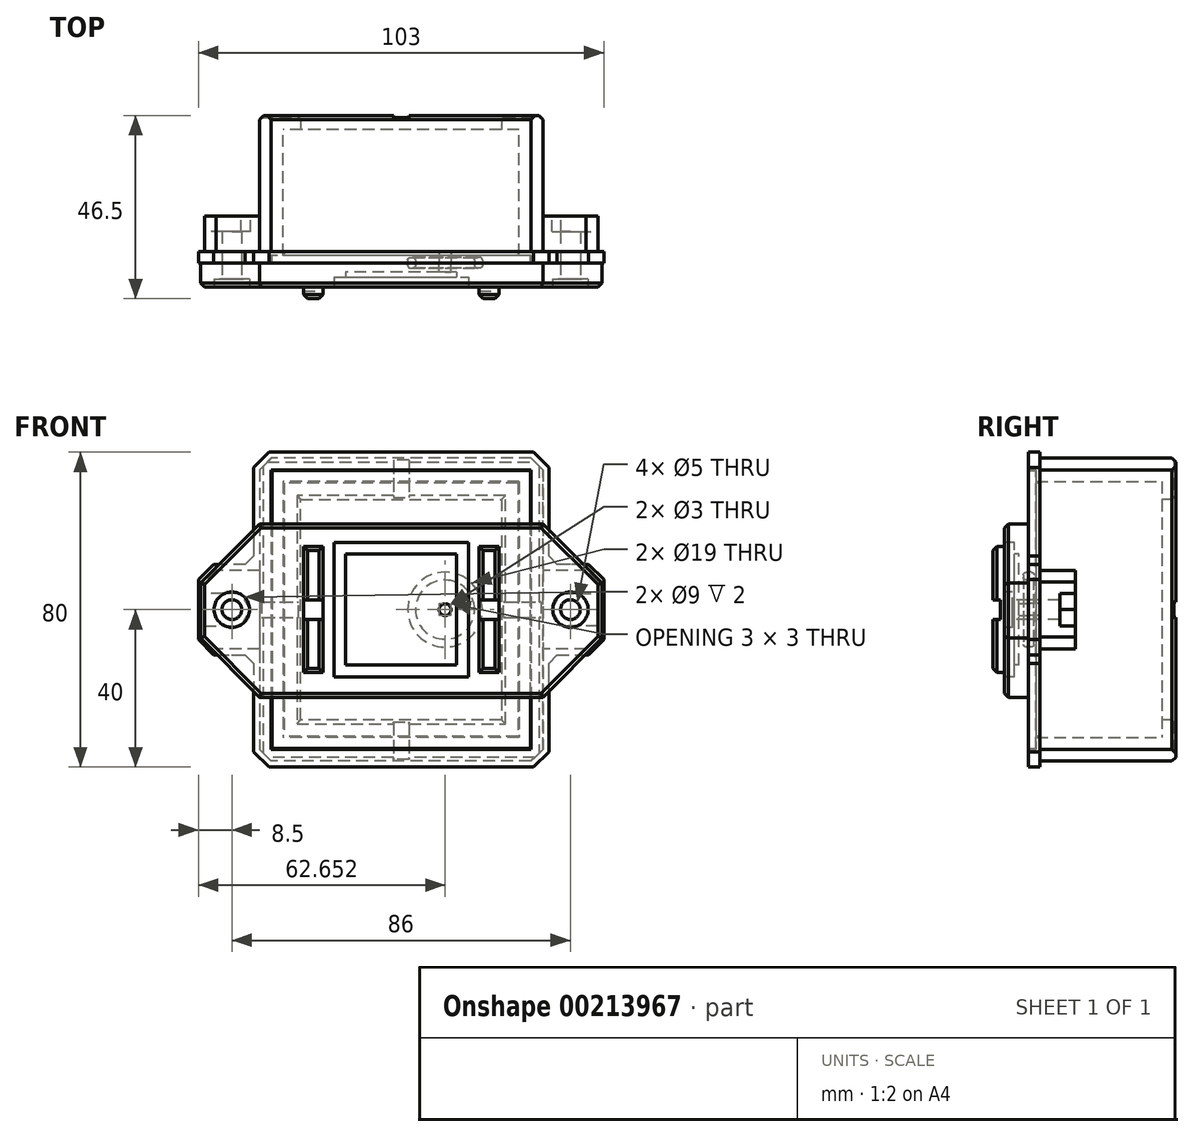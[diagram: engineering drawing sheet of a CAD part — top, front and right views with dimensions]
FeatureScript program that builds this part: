
annotation { "Feature Type Name" : "Feature", "Feature Type Description" : "" }
export const myFeature = defineFeature(function(context is Context, id is Id, definition is map)
    precondition{}
    {
        {
            var Q0;
            Q0=qCreatedBy(makeId("Front.planeOp"),FACE);
            var sketch = newSketch(context, id + "F0", { "sketchPlane" : qUnion([Q0])});
            skLineSegment(sketch, "E0.bottom", {"start": v(30, 32.5) * mm, "end": v(-30, 32.5) * mm});
            skLineSegment(sketch, "E0.top", {"start": v(30, -32.5) * mm, "end": v(-30, -32.5) * mm});
            skLineSegment(sketch, "E0.left", {"start": v(30, 32.5) * mm, "end": v(30, -32.5) * mm});
            skLineSegment(sketch, "E0.right", {"start": v(-30, 32.5) * mm, "end": v(-30, -32.5) * mm});
            skPoint(sketch, "E0.middle", {"position": v(0, 0) * mm});
            skLineSegment(sketch, "E1.0", {"start": v(36, -38.5) * mm, "end": v(-36, -38.5) * mm});
            skLineSegment(sketch, "E1.1", {"start": v(36, 38.5) * mm, "end": v(36, -38.5) * mm});
            skLineSegment(sketch, "E1.2", {"start": v(36, 38.5) * mm, "end": v(-36, 38.5) * mm});
            skLineSegment(sketch, "E1.3", {"start": v(-36, 38.5) * mm, "end": v(-36, -38.5) * mm});
            skSolve(sketch);
        }
        {
            var Q0;
            Q0 = qSketchRegion(id + "F0", true);
            extrude(context, id + "F1", {"entities" : qUnion([Q0]), "depth" : 34 * mm});
        }
        {
            var Q0;
            Q0=makeQuery(id+"F1.opExtrude","CAP_FACE",FACE,{"disambiguationData":[OSD([sQuery(id+"F0.wireOp",EDGE,"E0.bottom"),sQuery(id+"F0.wireOp",EDGE,"E0.top"),sQuery(id+"F0.wireOp",EDGE,"E0.left"),sQuery(id+"F0.wireOp",EDGE,"E0.right"),sQuery(id+"F0.wireOp",EDGE,"E1.0"),sQuery(id+"F0.wireOp",EDGE,"E1.1"),sQuery(id+"F0.wireOp",EDGE,"E1.2"),sQuery(id+"F0.wireOp",EDGE,"E1.3")])],"isStart":true});
            var sketch = newSketch(context, id + "F2", { "sketchPlane" : qUnion([Q0])});
            skLineSegment(sketch, "E2.bottom", {"start": v(-36, -38.5) * mm, "end": v(36, -38.5) * mm});
            skLineSegment(sketch, "E2.top", {"start": v(-36, 38.5) * mm, "end": v(36, 38.5) * mm});
            skLineSegment(sketch, "E2.left", {"start": v(-36, -38.5) * mm, "end": v(-36, 38.5) * mm});
            skLineSegment(sketch, "E2.right", {"start": v(36, -38.5) * mm, "end": v(36, 38.5) * mm});
            skLineSegment(sketch, "E3.0", {"start": v(-25.5, -28) * mm, "end": v(25.5, -28) * mm});
            skLineSegment(sketch, "E3.1", {"start": v(-25.5, 28) * mm, "end": v(-25.5, -28) * mm});
            skLineSegment(sketch, "E3.2", {"start": v(-25.5, 28) * mm, "end": v(25.5, 28) * mm});
            skLineSegment(sketch, "E3.3", {"start": v(25.5, 28) * mm, "end": v(25.5, -28) * mm});
            skSolve(sketch);
        }
        {
            var Q0;
            Q0 = qSketchRegion(id + "F2", true);
            extrude(context, id + "F3", {"entities" : qUnion([Q0]), "operationType" : NewBodyOperationType.ADD, "depth" : 3.5 * mm});
        }
        {
            var Q0;
            Q0=makeQuery(id+"F3.opExtrude","CAP_FACE",FACE,{"disambiguationData":[OSD([sQuery(id+"F2.wireOp",EDGE,"E2.bottom"),sQuery(id+"F2.wireOp",EDGE,"E2.top"),sQuery(id+"F2.wireOp",EDGE,"E2.left"),sQuery(id+"F2.wireOp",EDGE,"E2.right"),sQuery(id+"F2.wireOp",EDGE,"E3.0"),sQuery(id+"F2.wireOp",EDGE,"E3.1"),sQuery(id+"F2.wireOp",EDGE,"E3.2"),sQuery(id+"F2.wireOp",EDGE,"E3.3")])],"isStart":false});
            chamfer(context, id + "F4", {"entities" : qUnion([Q0]), "width" : 1 * mm, "tangentPropagation" : true});
        }
        {
            var Q0;
            Q0=makeQuery(id+"F3.boolean.opBoolean","MERGE",EDGE,{"derivedFrom":[makeQuery(id+"F1.opExtrude","SWEPT_EDGE",EDGE,{"disambiguationData":[OSD([sQuery(id+"F0.wireOp",EDGE,"E1.2"),sQuery(id+"F0.wireOp",EDGE,"E1.3")])]}),makeQuery(id+"F3.opExtrude","SWEPT_EDGE",EDGE,{"disambiguationData":[OSD([sQuery(id+"F2.wireOp",EDGE,"E2.top"),sQuery(id+"F2.wireOp",EDGE,"E2.right")])]})]});
            var Q1;
            Q1=makeQuery(id+"F3.boolean.opBoolean","MERGE",EDGE,{"derivedFrom":[makeQuery(id+"F1.opExtrude","SWEPT_EDGE",EDGE,{"disambiguationData":[OSD([sQuery(id+"F0.wireOp",EDGE,"E1.1"),sQuery(id+"F0.wireOp",EDGE,"E1.2")])]}),makeQuery(id+"F3.opExtrude","SWEPT_EDGE",EDGE,{"disambiguationData":[OSD([sQuery(id+"F2.wireOp",EDGE,"E2.top"),sQuery(id+"F2.wireOp",EDGE,"E2.left")])]})]});
            var Q2;
            Q2=makeQuery(id+"F3.boolean.opBoolean","MERGE",EDGE,{"derivedFrom":[makeQuery(id+"F1.opExtrude","SWEPT_EDGE",EDGE,{"disambiguationData":[OSD([sQuery(id+"F0.wireOp",EDGE,"E1.0"),sQuery(id+"F0.wireOp",EDGE,"E1.1")])]}),makeQuery(id+"F3.opExtrude","SWEPT_EDGE",EDGE,{"disambiguationData":[OSD([sQuery(id+"F2.wireOp",EDGE,"E2.bottom"),sQuery(id+"F2.wireOp",EDGE,"E2.left")])]})]});
            var Q3;
            Q3=makeQuery(id+"F3.boolean.opBoolean","MERGE",EDGE,{"derivedFrom":[makeQuery(id+"F1.opExtrude","SWEPT_EDGE",EDGE,{"disambiguationData":[OSD([sQuery(id+"F0.wireOp",EDGE,"E1.0"),sQuery(id+"F0.wireOp",EDGE,"E1.3")])]}),makeQuery(id+"F3.opExtrude","SWEPT_EDGE",EDGE,{"disambiguationData":[OSD([sQuery(id+"F2.wireOp",EDGE,"E2.bottom"),sQuery(id+"F2.wireOp",EDGE,"E2.right")])]})]});
            chamfer(context, id + "F5", {"entities" : qUnion([Q0, Q1, Q2, Q3]), "width" : 3 * mm, "tangentPropagation" : true});
        }
        {
            var Q0;
            Q0=makeQuery(id+"F1.opExtrude","CAP_FACE",FACE,{"disambiguationData":[OSD([sQuery(id+"F0.wireOp",EDGE,"E0.bottom"),sQuery(id+"F0.wireOp",EDGE,"E0.top"),sQuery(id+"F0.wireOp",EDGE,"E0.left"),sQuery(id+"F0.wireOp",EDGE,"E0.right"),sQuery(id+"F0.wireOp",EDGE,"E1.0"),sQuery(id+"F0.wireOp",EDGE,"E1.1"),sQuery(id+"F0.wireOp",EDGE,"E1.2"),sQuery(id+"F0.wireOp",EDGE,"E1.3")])],"isStart":false});
            var sketch = newSketch(context, id + "F6", { "sketchPlane" : qUnion([Q0])});
            skLineSegment(sketch, "E4", {"start": v(0, 0) * mm, "end": v(-36, 0) * mm, "construction": true});
            skLineSegment(sketch, "E5.bottom", {"start": v(-50, -10) * mm, "end": v(-36, -10) * mm});
            skLineSegment(sketch, "E5.top", {"start": v(-50, 10) * mm, "end": v(-36, 10) * mm});
            skLineSegment(sketch, "E5.left", {"start": v(-50, -10) * mm, "end": v(-50, 10) * mm});
            skLineSegment(sketch, "E5.right", {"start": v(-36, -10) * mm, "end": v(-36, 10) * mm});
            skPoint(sketch, "E5.middle", {"position": v(-43, 0) * mm});
            skSolve(sketch);
        }
        {
            var Q0;
            Q0 = qSketchRegion(id + "F6", true);
            extrude(context, id + "F7", {"entities" : qUnion([Q0]), "oppositeDirection" : true, "depth" : 12 * mm});
        }
        {
            var Q0;
            Q0=makeQuery(id+"F7.opExtrude","CAP_FACE",FACE,{"disambiguationData":[OSD([sQuery(id+"F6.wireOp",EDGE,"E5.bottom"),sQuery(id+"F6.wireOp",EDGE,"E5.top"),sQuery(id+"F6.wireOp",EDGE,"E5.left"),sQuery(id+"F6.wireOp",EDGE,"E5.right")])],"isStart":false});
            var sketch = newSketch(context, id + "F8", { "sketchPlane" : qUnion([Q0])});
            skLineSegment(sketch, "E6", {"start": v(50, 0) * mm, "end": v(43, 0) * mm, "construction": true});
            skPoint(sketch, "E6.endSnap0", {"position": v(50, 0) * mm});
            skCircle(sketch, "E7.cCircle", {"center": v(43, 0) * mm, "radius": 4.1 * mm, "construction": true});
            skLineSegment(sketch, "E7.0", {"start": v(45.37, -4.1) * mm, "end": v(40.63, -4.1) * mm});
            skLineSegment(sketch, "E7.1", {"start": v(40.63, -4.1) * mm, "end": v(38.27, 0) * mm});
            skLineSegment(sketch, "E7.2", {"start": v(38.27, 0) * mm, "end": v(40.63, 4.1) * mm});
            skLineSegment(sketch, "E7.3", {"start": v(40.63, 4.1) * mm, "end": v(45.37, 4.1) * mm});
            skLineSegment(sketch, "E7.4", {"start": v(45.37, 4.1) * mm, "end": v(47.73, 0) * mm, "construction": true});
            skLineSegment(sketch, "E7.5", {"start": v(47.73, 0) * mm, "end": v(45.37, -4.1) * mm, "construction": true});
            skPoint(sketch, "E7.0.midPoint", {"position": v(43, -4.1) * mm});
            skLineSegment(sketch, "E8.bottom", {"start": v(45.37, 4.1) * mm, "end": v(50, 4.1) * mm});
            skLineSegment(sketch, "E8.top", {"start": v(45.37, -4.1) * mm, "end": v(50, -4.1) * mm});
            skLineSegment(sketch, "E8.left", {"start": v(45.37, 4.1) * mm, "end": v(45.37, -4.1) * mm, "construction": true});
            skLineSegment(sketch, "E8.right", {"start": v(50, 4.1) * mm, "end": v(50, -4.1) * mm});
            skSolve(sketch);
        }
        {
            var Q0;
            Q0 = qSketchRegion(id + "F8", true);
            extrude(context, id + "F9", {"entities" : qUnion([Q0]), "operationType" : NewBodyOperationType.REMOVE, "oppositeDirection" : true, "depth" : 4 * mm});
        }
        {
            var Q0;
            Q0=makeQuery(id+"F7.boolean.opBoolean","MERGE",FACE,{"derivedFrom":[makeQuery(id+"F1.opExtrude","CAP_FACE",FACE,{"disambiguationData":[OSD([sQuery(id+"F0.wireOp",EDGE,"E0.bottom"),sQuery(id+"F0.wireOp",EDGE,"E0.top"),sQuery(id+"F0.wireOp",EDGE,"E0.left"),sQuery(id+"F0.wireOp",EDGE,"E0.right"),sQuery(id+"F0.wireOp",EDGE,"E1.0"),sQuery(id+"F0.wireOp",EDGE,"E1.1"),sQuery(id+"F0.wireOp",EDGE,"E1.2"),sQuery(id+"F0.wireOp",EDGE,"E1.3")])],"isStart":false}),makeQuery(id+"F7.opExtrude","CAP_FACE",FACE,{"disambiguationData":[OSD([sQuery(id+"F6.wireOp",EDGE,"E5.bottom"),sQuery(id+"F6.wireOp",EDGE,"E5.top"),sQuery(id+"F6.wireOp",EDGE,"E5.left"),sQuery(id+"F6.wireOp",EDGE,"E5.right")])],"isStart":true})]});
            var sketch = newSketch(context, id + "F10", { "sketchPlane" : qUnion([Q0])});
            skLineSegment(sketch, "E9", {"start": v(0, 0) * mm, "end": v(-43, 0) * mm, "construction": true});
            skCircle(sketch, "E10", {"center": v(-43, 0) * mm, "radius": 2.5 * mm});
            skSolve(sketch);
        }
        {
            var Q0;
            Q0 = qSketchRegion(id + "F10", true);
            extrude(context, id + "F11", {"entities" : qUnion([Q0]), "operationType" : NewBodyOperationType.REMOVE, "endBound" : BoundingType.THROUGH_ALL, "oppositeDirection" : true, "depth" : 25 * mm});
        }
        {
            var Q0;
            Q0=makeQuery(id+"F7.opExtrude","SWEPT_BODY",BODY,{"disambiguationData":[OSD([sQuery(id+"F6.wireOp",EDGE,"E5.bottom"),sQuery(id+"F6.wireOp",EDGE,"E5.top"),sQuery(id+"F6.wireOp",EDGE,"E5.left"),sQuery(id+"F6.wireOp",EDGE,"E5.right")])]});
            var Q1;
            Q1=qCreatedBy(makeId("Right.planeOp"),FACE);
            mirror(context, id + "F12", {"operationType" : NewBodyOperationType.ADD, "entities" : qUnion([Q0]), "mirrorPlane" : qUnion([Q1])});
        }
        {
            var Q0;
            Q0=makeQuery(id+"F12.opPattern","COPY",EDGE,{"derivedFrom":makeQuery(id+"F7.opExtrude","SWEPT_EDGE",EDGE,{"disambiguationData":[OSD([sQuery(id+"F6.wireOp",EDGE,"E5.bottom"),sQuery(id+"F6.wireOp",EDGE,"E5.left")])]}),"instanceName":"1"});
            var Q1;
            Q1=makeQuery(id+"F12.opPattern","COPY",EDGE,{"derivedFrom":makeQuery(id+"F7.opExtrude","SWEPT_EDGE",EDGE,{"disambiguationData":[OSD([sQuery(id+"F0.wireOp",EDGE,"E1.3"),sQuery(id+"F6.wireOp",EDGE,"E5.bottom"),sQuery(id+"F6.wireOp",EDGE,"E5.right")])]}),"instanceName":"1"});
            var Q2;
            Q2=makeQuery(id+"F12.opPattern","COPY",EDGE,{"derivedFrom":makeQuery(id+"F7.opExtrude","SWEPT_EDGE",EDGE,{"disambiguationData":[OSD([sQuery(id+"F6.wireOp",EDGE,"E5.top"),sQuery(id+"F6.wireOp",EDGE,"E5.left")])]}),"instanceName":"1"});
            var Q3;
            Q3=makeQuery(id+"F12.opPattern","COPY",EDGE,{"derivedFrom":makeQuery(id+"F7.opExtrude","SWEPT_EDGE",EDGE,{"disambiguationData":[OSD([sQuery(id+"F0.wireOp",EDGE,"E1.3"),sQuery(id+"F6.wireOp",EDGE,"E5.top"),sQuery(id+"F6.wireOp",EDGE,"E5.right")])]}),"instanceName":"1"});
            var Q4;
            Q4=makeQuery(id+"F7.opExtrude","SWEPT_EDGE",EDGE,{"disambiguationData":[OSD([sQuery(id+"F0.wireOp",EDGE,"E1.3"),sQuery(id+"F6.wireOp",EDGE,"E5.top"),sQuery(id+"F6.wireOp",EDGE,"E5.right")])]});
            var Q5;
            Q5=makeQuery(id+"F7.opExtrude","SWEPT_EDGE",EDGE,{"disambiguationData":[OSD([sQuery(id+"F6.wireOp",EDGE,"E5.top"),sQuery(id+"F6.wireOp",EDGE,"E5.left")])]});
            var Q6;
            Q6=makeQuery(id+"F7.opExtrude","SWEPT_EDGE",EDGE,{"disambiguationData":[OSD([sQuery(id+"F0.wireOp",EDGE,"E1.3"),sQuery(id+"F6.wireOp",EDGE,"E5.bottom"),sQuery(id+"F6.wireOp",EDGE,"E5.right")])]});
            var Q7;
            Q7=makeQuery(id+"F7.opExtrude","SWEPT_EDGE",EDGE,{"disambiguationData":[OSD([sQuery(id+"F6.wireOp",EDGE,"E5.bottom"),sQuery(id+"F6.wireOp",EDGE,"E5.left")])]});
            chamfer(context, id + "F13", {"entities" : qUnion([Q0, Q1, Q2, Q3, Q4, Q5, Q6, Q7]), "width" : 3 * mm, "tangentPropagation" : true});
        }
        {
            var Q0;
            Q0=makeQuery(id+"F3.opExtrude","CAP_FACE",FACE,{"disambiguationData":[OSD([sQuery(id+"F2.wireOp",EDGE,"E2.bottom"),sQuery(id+"F2.wireOp",EDGE,"E2.top"),sQuery(id+"F2.wireOp",EDGE,"E2.left"),sQuery(id+"F2.wireOp",EDGE,"E2.right"),sQuery(id+"F2.wireOp",EDGE,"E3.0"),sQuery(id+"F2.wireOp",EDGE,"E3.1"),sQuery(id+"F2.wireOp",EDGE,"E3.2"),sQuery(id+"F2.wireOp",EDGE,"E3.3")])],"isStart":false});
            var sketch = newSketch(context, id + "F14", { "sketchPlane" : qUnion([Q0])});
            skLineSegment(sketch, "E11.bottom", {"start": v(2, 48.52) * mm, "end": v(-2, 48.52) * mm});
            skLineSegment(sketch, "E11.top", {"start": v(2, -48.52) * mm, "end": v(-2, -48.52) * mm});
            skLineSegment(sketch, "E11.left", {"start": v(2, 48.52) * mm, "end": v(2, -48.52) * mm});
            skLineSegment(sketch, "E11.right", {"start": v(-2, 48.52) * mm, "end": v(-2, -48.52) * mm});
            skPoint(sketch, "E11.middle", {"position": v(0, 0) * mm});
            skLineSegment(sketch, "E12.bottom", {"start": v(65.48, 2) * mm, "end": v(-65.48, 2) * mm});
            skLineSegment(sketch, "E12.top", {"start": v(65.48, -2) * mm, "end": v(-65.48, -2) * mm});
            skLineSegment(sketch, "E12.left", {"start": v(65.48, 2) * mm, "end": v(65.48, -2) * mm});
            skLineSegment(sketch, "E12.right", {"start": v(-65.48, 2) * mm, "end": v(-65.48, -2) * mm});
            skSolve(sketch);
        }
        {
            var Q0;
            Q0 = qSketchRegion(id + "F14", true);
            extrude(context, id + "F15", {"entities" : qUnion([Q0]), "operationType" : NewBodyOperationType.REMOVE, "oppositeDirection" : true, "depth" : 0.5 * mm});
        }
        {
            var Q0;
            {var subQ0=makeQuery(id+"F7.opExtrude","CAP_FACE",FACE,{"disambiguationData":[OSD([sQuery(id+"F6.wireOp",EDGE,"E5.bottom"),sQuery(id+"F6.wireOp",EDGE,"E5.top"),sQuery(id+"F6.wireOp",EDGE,"E5.left"),sQuery(id+"F6.wireOp",EDGE,"E5.right")])],"isStart":true});Q0=makeQuery(id+"F12.boolean.opBoolean","MERGE",FACE,{"derivedFrom":[makeQuery(id+"F1.opExtrude","CAP_FACE",FACE,{"disambiguationData":[OSD([sQuery(id+"F0.wireOp",EDGE,"E0.bottom"),sQuery(id+"F0.wireOp",EDGE,"E0.top"),sQuery(id+"F0.wireOp",EDGE,"E0.left"),sQuery(id+"F0.wireOp",EDGE,"E0.right"),sQuery(id+"F0.wireOp",EDGE,"E1.0"),sQuery(id+"F0.wireOp",EDGE,"E1.1"),sQuery(id+"F0.wireOp",EDGE,"E1.2"),sQuery(id+"F0.wireOp",EDGE,"E1.3")])],"isStart":false}),subQ0,makeQuery(id+"F12.opPattern","COPY",FACE,{"derivedFrom":subQ0,"instanceName":"1"})]});}
            var sketch = newSketch(context, id + "F16", { "sketchPlane" : qUnion([Q0])});
            skLineSegment(sketch, "E13.0", {"start": v(-47.62, 11.5) * mm, "end": v(-51.5, 7.62) * mm});
            skLineSegment(sketch, "E13.1", {"start": v(39.62, -11.5) * mm, "end": v(47.62, -11.5) * mm});
            skLineSegment(sketch, "E13.2", {"start": v(37.5, -13.62) * mm, "end": v(39.62, -11.5) * mm});
            skLineSegment(sketch, "E13.3", {"start": v(37.5, -36.12) * mm, "end": v(37.5, -13.62) * mm});
            skLineSegment(sketch, "E13.4", {"start": v(33.62, -40) * mm, "end": v(37.5, -36.12) * mm});
            skLineSegment(sketch, "E13.5", {"start": v(-33.62, -40) * mm, "end": v(33.62, -40) * mm});
            skLineSegment(sketch, "E13.6", {"start": v(-37.5, -36.12) * mm, "end": v(-33.62, -40) * mm});
            skLineSegment(sketch, "E13.7", {"start": v(-51.5, -7.62) * mm, "end": v(-47.62, -11.5) * mm});
            skLineSegment(sketch, "E13.8", {"start": v(-47.62, -11.5) * mm, "end": v(-39.62, -11.5) * mm});
            skLineSegment(sketch, "E13.9", {"start": v(-39.62, -11.5) * mm, "end": v(-37.5, -13.62) * mm});
            skLineSegment(sketch, "E13.10", {"start": v(-37.5, -13.62) * mm, "end": v(-37.5, -36.12) * mm});
            skLineSegment(sketch, "E13.11", {"start": v(47.62, -11.5) * mm, "end": v(51.5, -7.62) * mm});
            skLineSegment(sketch, "E13.12", {"start": v(-51.5, 7.62) * mm, "end": v(-51.5, -7.62) * mm});
            skLineSegment(sketch, "E13.13", {"start": v(51.5, -7.62) * mm, "end": v(51.5, 7.62) * mm});
            skLineSegment(sketch, "E13.14", {"start": v(51.5, 7.62) * mm, "end": v(47.62, 11.5) * mm});
            skLineSegment(sketch, "E13.15", {"start": v(47.62, 11.5) * mm, "end": v(39.62, 11.5) * mm});
            skLineSegment(sketch, "E13.16", {"start": v(39.62, 11.5) * mm, "end": v(37.5, 13.62) * mm});
            skLineSegment(sketch, "E13.17", {"start": v(37.5, 13.62) * mm, "end": v(37.5, 36.12) * mm});
            skLineSegment(sketch, "E13.18", {"start": v(37.5, 36.12) * mm, "end": v(33.62, 40) * mm});
            skLineSegment(sketch, "E13.19", {"start": v(33.62, 40) * mm, "end": v(-33.62, 40) * mm});
            skLineSegment(sketch, "E13.20", {"start": v(-33.62, 40) * mm, "end": v(-37.5, 36.12) * mm});
            skLineSegment(sketch, "E13.21", {"start": v(-37.5, 36.12) * mm, "end": v(-37.5, 13.62) * mm});
            skLineSegment(sketch, "E13.22", {"start": v(-37.5, 13.62) * mm, "end": v(-39.62, 11.5) * mm});
            skLineSegment(sketch, "E13.23", {"start": v(-39.62, 11.5) * mm, "end": v(-47.62, 11.5) * mm});
            skCircle(sketch, "E14.0", {"center": v(-43, 0) * mm, "radius": 2.5 * mm});
            skCircle(sketch, "E15.0", {"center": v(43, 0) * mm, "radius": 2.5 * mm});
            skLineSegment(sketch, "E16.0", {"start": v(-30, 32.5) * mm, "end": v(-30, -32.5) * mm});
            skLineSegment(sketch, "E16.1", {"start": v(30, -32.5) * mm, "end": v(-30, -32.5) * mm});
            skLineSegment(sketch, "E16.2", {"start": v(30, 32.5) * mm, "end": v(-30, 32.5) * mm});
            skLineSegment(sketch, "E16.3", {"start": v(30, 32.5) * mm, "end": v(30, -32.5) * mm});
            skSolve(sketch);
        }
        {
            var Q0;
            Q0 = qSketchRegion(id + "F16", true);
            extrude(context, id + "F17", {"entities" : qUnion([Q0]), "operationType" : NewBodyOperationType.ADD, "oppositeDirection" : true, "depth" : 3 * mm});
        }
        {
            var Q0;
            {var subQ0=makeQuery(id+"F7.opExtrude","CAP_FACE",FACE,{"disambiguationData":[OSD([sQuery(id+"F6.wireOp",EDGE,"E5.bottom"),sQuery(id+"F6.wireOp",EDGE,"E5.top"),sQuery(id+"F6.wireOp",EDGE,"E5.left"),sQuery(id+"F6.wireOp",EDGE,"E5.right")])],"isStart":true});Q0=makeQuery(id+"F17.boolean.opBoolean","MERGE",FACE,{"derivedFrom":[makeQuery(id+"F12.boolean.opBoolean","MERGE",FACE,{"derivedFrom":[makeQuery(id+"F1.opExtrude","CAP_FACE",FACE,{"disambiguationData":[OSD([sQuery(id+"F0.wireOp",EDGE,"E0.bottom"),sQuery(id+"F0.wireOp",EDGE,"E0.top"),sQuery(id+"F0.wireOp",EDGE,"E0.left"),sQuery(id+"F0.wireOp",EDGE,"E0.right"),sQuery(id+"F0.wireOp",EDGE,"E1.0"),sQuery(id+"F0.wireOp",EDGE,"E1.1"),sQuery(id+"F0.wireOp",EDGE,"E1.2"),sQuery(id+"F0.wireOp",EDGE,"E1.3")])],"isStart":false}),subQ0,makeQuery(id+"F12.opPattern","COPY",FACE,{"derivedFrom":subQ0,"instanceName":"1"})]}),makeQuery(id+"F17.opExtrude","CAP_FACE",FACE,{"disambiguationData":[OSD([sQuery(id+"F16.wireOp",EDGE,"E13.0"),sQuery(id+"F16.wireOp",EDGE,"E13.1"),sQuery(id+"F16.wireOp",EDGE,"E13.2"),sQuery(id+"F16.wireOp",EDGE,"E13.3"),sQuery(id+"F16.wireOp",EDGE,"E13.4"),sQuery(id+"F16.wireOp",EDGE,"E13.5"),sQuery(id+"F16.wireOp",EDGE,"E13.6"),sQuery(id+"F16.wireOp",EDGE,"E13.7"),sQuery(id+"F16.wireOp",EDGE,"E13.8"),sQuery(id+"F16.wireOp",EDGE,"E13.9"),sQuery(id+"F16.wireOp",EDGE,"E13.10"),sQuery(id+"F16.wireOp",EDGE,"E13.11"),sQuery(id+"F16.wireOp",EDGE,"E13.12"),sQuery(id+"F16.wireOp",EDGE,"E13.13"),sQuery(id+"F16.wireOp",EDGE,"E13.14"),sQuery(id+"F16.wireOp",EDGE,"E13.15"),sQuery(id+"F16.wireOp",EDGE,"E13.16"),sQuery(id+"F16.wireOp",EDGE,"E13.17"),sQuery(id+"F16.wireOp",EDGE,"E13.18"),sQuery(id+"F16.wireOp",EDGE,"E13.19"),sQuery(id+"F16.wireOp",EDGE,"E13.20"),sQuery(id+"F16.wireOp",EDGE,"E13.21"),sQuery(id+"F16.wireOp",EDGE,"E13.22"),sQuery(id+"F16.wireOp",EDGE,"E13.23"),sQuery(id+"F16.wireOp",EDGE,"E14.0"),sQuery(id+"F16.wireOp",EDGE,"E15.0"),sQuery(id+"F16.wireOp",EDGE,"E16.0"),sQuery(id+"F16.wireOp",EDGE,"E16.1"),sQuery(id+"F16.wireOp",EDGE,"E16.2"),sQuery(id+"F16.wireOp",EDGE,"E16.3")])],"isStart":true})]});}
            var sketch = newSketch(context, id + "F18", { "sketchPlane" : qUnion([Q0])});
            skLineSegment(sketch, "E17.0", {"start": v(33, 35.5) * mm, "end": v(-33, 35.5) * mm});
            skLineSegment(sketch, "E17.1", {"start": v(33, 35.5) * mm, "end": v(33, -35.5) * mm});
            skLineSegment(sketch, "E17.2", {"start": v(33, -35.5) * mm, "end": v(-33, -35.5) * mm});
            skLineSegment(sketch, "E17.3", {"start": v(-33, 35.5) * mm, "end": v(-33, -35.5) * mm});
            skSolve(sketch);
        }
        {
            var Q0;
            Q0 = qSketchRegion(id + "F18", true);
            extrude(context, id + "F19", {"entities" : qUnion([Q0]), "operationType" : NewBodyOperationType.REMOVE, "oppositeDirection" : true, "depth" : 2 * mm});
        }
        {
            var Q0;
            Q0=makeQuery(id+"F19.boolean.opBoolean","COPY",FACE,{"derivedFrom":makeQuery(id+"F19.opExtrude","CAP_FACE",FACE,{"disambiguationData":[OSD([sQuery(id+"F18.wireOp",EDGE,"E17.0"),sQuery(id+"F18.wireOp",EDGE,"E17.1"),sQuery(id+"F18.wireOp",EDGE,"E17.2"),sQuery(id+"F18.wireOp",EDGE,"E17.3")])],"isStart":false})});
            var sketch = newSketch(context, id + "F20", { "sketchPlane" : qUnion([Q0])});
            skLineSegment(sketch, "E18.0", {"start": v(32.8, 35.3) * mm, "end": v(-32.8, 35.3) * mm});
            skLineSegment(sketch, "E18.1", {"start": v(32.8, -35.3) * mm, "end": v(32.8, 35.3) * mm});
            skLineSegment(sketch, "E18.2", {"start": v(-32.8, -35.3) * mm, "end": v(32.8, -35.3) * mm});
            skLineSegment(sketch, "E18.3", {"start": v(-32.8, 35.3) * mm, "end": v(-32.8, -35.3) * mm});
            skSolve(sketch);
        }
        {
            var Q0;
            Q0 = qSketchRegion(id + "F20", true);
            var Q1;
            {var subQ0=makeQuery(id+"F7.opExtrude","CAP_FACE",FACE,{"disambiguationData":[OSD([sQuery(id+"F6.wireOp",EDGE,"E5.bottom"),sQuery(id+"F6.wireOp",EDGE,"E5.top"),sQuery(id+"F6.wireOp",EDGE,"E5.left"),sQuery(id+"F6.wireOp",EDGE,"E5.right")])],"isStart":true});Q1=makeQuery(id+"F17.boolean.opBoolean","MERGE",FACE,{"derivedFrom":[makeQuery(id+"F12.boolean.opBoolean","MERGE",FACE,{"derivedFrom":[makeQuery(id+"F1.opExtrude","CAP_FACE",FACE,{"disambiguationData":[OSD([sQuery(id+"F0.wireOp",EDGE,"E0.bottom"),sQuery(id+"F0.wireOp",EDGE,"E0.top"),sQuery(id+"F0.wireOp",EDGE,"E0.left"),sQuery(id+"F0.wireOp",EDGE,"E0.right"),sQuery(id+"F0.wireOp",EDGE,"E1.0"),sQuery(id+"F0.wireOp",EDGE,"E1.1"),sQuery(id+"F0.wireOp",EDGE,"E1.2"),sQuery(id+"F0.wireOp",EDGE,"E1.3")])],"isStart":false}),subQ0,makeQuery(id+"F12.opPattern","COPY",FACE,{"derivedFrom":subQ0,"instanceName":"1"})]}),makeQuery(id+"F17.opExtrude","CAP_FACE",FACE,{"disambiguationData":[OSD([sQuery(id+"F16.wireOp",EDGE,"E13.0"),sQuery(id+"F16.wireOp",EDGE,"E13.1"),sQuery(id+"F16.wireOp",EDGE,"E13.2"),sQuery(id+"F16.wireOp",EDGE,"E13.3"),sQuery(id+"F16.wireOp",EDGE,"E13.4"),sQuery(id+"F16.wireOp",EDGE,"E13.5"),sQuery(id+"F16.wireOp",EDGE,"E13.6"),sQuery(id+"F16.wireOp",EDGE,"E13.7"),sQuery(id+"F16.wireOp",EDGE,"E13.8"),sQuery(id+"F16.wireOp",EDGE,"E13.9"),sQuery(id+"F16.wireOp",EDGE,"E13.10"),sQuery(id+"F16.wireOp",EDGE,"E13.11"),sQuery(id+"F16.wireOp",EDGE,"E13.12"),sQuery(id+"F16.wireOp",EDGE,"E13.13"),sQuery(id+"F16.wireOp",EDGE,"E13.14"),sQuery(id+"F16.wireOp",EDGE,"E13.15"),sQuery(id+"F16.wireOp",EDGE,"E13.16"),sQuery(id+"F16.wireOp",EDGE,"E13.17"),sQuery(id+"F16.wireOp",EDGE,"E13.18"),sQuery(id+"F16.wireOp",EDGE,"E13.19"),sQuery(id+"F16.wireOp",EDGE,"E13.20"),sQuery(id+"F16.wireOp",EDGE,"E13.21"),sQuery(id+"F16.wireOp",EDGE,"E13.22"),sQuery(id+"F16.wireOp",EDGE,"E13.23"),sQuery(id+"F16.wireOp",EDGE,"E14.0"),sQuery(id+"F16.wireOp",EDGE,"E15.0"),sQuery(id+"F16.wireOp",EDGE,"E16.0"),sQuery(id+"F16.wireOp",EDGE,"E16.1"),sQuery(id+"F16.wireOp",EDGE,"E16.2"),sQuery(id+"F16.wireOp",EDGE,"E16.3")])],"isStart":true})]});}
            extrude(context, id + "F21", {"entities" : qUnion([Q0]), "endBound" : BoundingType.UP_TO_SURFACE, "endBoundEntityFace" : qUnion([Q1]), "depth" : 25 * mm});
        }
        {
            var Q0;
            Q0=makeQuery(id+"F21.opExtrude","CAP_FACE",FACE,{"disambiguationData":[OSD([sQuery(id+"F20.wireOp",EDGE,"E18.0"),sQuery(id+"F20.wireOp",EDGE,"E18.1"),sQuery(id+"F20.wireOp",EDGE,"E18.2"),sQuery(id+"F20.wireOp",EDGE,"E18.3")])],"isStart":true});
            var sketch = newSketch(context, id + "F22", { "sketchPlane" : qUnion([Q0])});
            skLineSegment(sketch, "E19.0", {"start": v(-29.7, 32.2) * mm, "end": v(29.7, 32.2) * mm});
            skLineSegment(sketch, "E19.1", {"start": v(-29.7, 32.2) * mm, "end": v(-29.7, -32.2) * mm});
            skLineSegment(sketch, "E19.2", {"start": v(-29.7, -32.2) * mm, "end": v(29.7, -32.2) * mm});
            skLineSegment(sketch, "E19.3", {"start": v(29.7, 32.2) * mm, "end": v(29.7, -32.2) * mm});
            skSolve(sketch);
        }
        {
            var Q0;
            Q0 = qSketchRegion(id + "F22", true);
            extrude(context, id + "F23", {"entities" : qUnion([Q0]), "operationType" : NewBodyOperationType.ADD, "depth" : 1 * mm});
        }
        {
            var Q0;
            Q0=makeQuery(id+"F21.opExtrude","CAP_FACE",FACE,{"disambiguationData":[OSD([sQuery(id+"F20.wireOp",EDGE,"E18.0"),sQuery(id+"F20.wireOp",EDGE,"E18.1"),sQuery(id+"F20.wireOp",EDGE,"E18.2"),sQuery(id+"F20.wireOp",EDGE,"E18.3")])],"isStart":false});
            var sketch = newSketch(context, id + "F24", { "sketchPlane" : qUnion([Q0])});
            skCircle(sketch, "E20", {"center": v(11.15, 0) * mm, "radius": 1.5 * mm});
            skSolve(sketch);
        }
        {
            var Q0;
            Q0 = qSketchRegion(id + "F24", true);
            extrude(context, id + "F25", {"entities" : qUnion([Q0]), "operationType" : NewBodyOperationType.REMOVE, "endBound" : BoundingType.THROUGH_ALL, "oppositeDirection" : true, "depth" : 25 * mm});
        }
        {
            var Q0;
            Q0=makeQuery(id+"F21.opExtrude","CAP_FACE",FACE,{"disambiguationData":[OSD([sQuery(id+"F20.wireOp",EDGE,"E18.0"),sQuery(id+"F20.wireOp",EDGE,"E18.1"),sQuery(id+"F20.wireOp",EDGE,"E18.2"),sQuery(id+"F20.wireOp",EDGE,"E18.3")])],"isStart":false});
            var sketch = newSketch(context, id + "F26", { "sketchPlane" : qUnion([Q0])});
            skCircle(sketch, "E21", {"center": v(11.15, 0) * mm, "radius": 7.5 * mm});
            skCircle(sketch, "E22", {"center": v(11.15, 0) * mm, "radius": 9.5 * mm});
            skSolve(sketch);
        }
        {
            var Q0;
            Q0 = qSketchRegion(id + "F26", true);
            extrude(context, id + "F27", {"entities" : qUnion([Q0]), "operationType" : NewBodyOperationType.REMOVE, "oppositeDirection" : true, "depth" : 1.5 * mm});
        }
        {
            var Q0;
            Q0=makeQuery(id+"F27.boolean.opBoolean","COPY",FACE,{"derivedFrom":makeQuery(id+"F27.opExtrude","CAP_FACE",FACE,{"disambiguationData":[OSD([sQuery(id+"F26.wireOp",EDGE,"E21"),sQuery(id+"F26.wireOp",EDGE,"E22")])],"isStart":false})});
            fillet(context, id + "F28", {"entities" : qUnion([Q0]), "radius" : 0.7 * mm, "tangentPropagation" : true, "allowEdgeOverflow" : false});
        }
        {
            var Q0;
            {var subQ0=makeQuery(id+"F7.opExtrude","CAP_FACE",FACE,{"disambiguationData":[OSD([sQuery(id+"F6.wireOp",EDGE,"E5.bottom"),sQuery(id+"F6.wireOp",EDGE,"E5.top"),sQuery(id+"F6.wireOp",EDGE,"E5.left"),sQuery(id+"F6.wireOp",EDGE,"E5.right")])],"isStart":true});Q0=makeQuery(id+"F17.boolean.opBoolean","MERGE",FACE,{"derivedFrom":[makeQuery(id+"F12.boolean.opBoolean","MERGE",FACE,{"derivedFrom":[makeQuery(id+"F1.opExtrude","CAP_FACE",FACE,{"disambiguationData":[OSD([sQuery(id+"F0.wireOp",EDGE,"E0.bottom"),sQuery(id+"F0.wireOp",EDGE,"E0.top"),sQuery(id+"F0.wireOp",EDGE,"E0.left"),sQuery(id+"F0.wireOp",EDGE,"E0.right"),sQuery(id+"F0.wireOp",EDGE,"E1.0"),sQuery(id+"F0.wireOp",EDGE,"E1.1"),sQuery(id+"F0.wireOp",EDGE,"E1.2"),sQuery(id+"F0.wireOp",EDGE,"E1.3")])],"isStart":false}),subQ0,makeQuery(id+"F12.opPattern","COPY",FACE,{"derivedFrom":subQ0,"instanceName":"1"})]}),makeQuery(id+"F17.opExtrude","CAP_FACE",FACE,{"disambiguationData":[OSD([sQuery(id+"F16.wireOp",EDGE,"E13.0"),sQuery(id+"F16.wireOp",EDGE,"E13.1"),sQuery(id+"F16.wireOp",EDGE,"E13.2"),sQuery(id+"F16.wireOp",EDGE,"E13.3"),sQuery(id+"F16.wireOp",EDGE,"E13.4"),sQuery(id+"F16.wireOp",EDGE,"E13.5"),sQuery(id+"F16.wireOp",EDGE,"E13.6"),sQuery(id+"F16.wireOp",EDGE,"E13.7"),sQuery(id+"F16.wireOp",EDGE,"E13.8"),sQuery(id+"F16.wireOp",EDGE,"E13.9"),sQuery(id+"F16.wireOp",EDGE,"E13.10"),sQuery(id+"F16.wireOp",EDGE,"E13.11"),sQuery(id+"F16.wireOp",EDGE,"E13.12"),sQuery(id+"F16.wireOp",EDGE,"E13.13"),sQuery(id+"F16.wireOp",EDGE,"E13.14"),sQuery(id+"F16.wireOp",EDGE,"E13.15"),sQuery(id+"F16.wireOp",EDGE,"E13.16"),sQuery(id+"F16.wireOp",EDGE,"E13.17"),sQuery(id+"F16.wireOp",EDGE,"E13.18"),sQuery(id+"F16.wireOp",EDGE,"E13.19"),sQuery(id+"F16.wireOp",EDGE,"E13.20"),sQuery(id+"F16.wireOp",EDGE,"E13.21"),sQuery(id+"F16.wireOp",EDGE,"E13.22"),sQuery(id+"F16.wireOp",EDGE,"E13.23"),sQuery(id+"F16.wireOp",EDGE,"E14.0"),sQuery(id+"F16.wireOp",EDGE,"E15.0"),sQuery(id+"F16.wireOp",EDGE,"E16.0"),sQuery(id+"F16.wireOp",EDGE,"E16.1"),sQuery(id+"F16.wireOp",EDGE,"E16.2"),sQuery(id+"F16.wireOp",EDGE,"E16.3")])],"isStart":true})]});}
            var sketch = newSketch(context, id + "F29", { "sketchPlane" : qUnion([Q0])});
            skLineSegment(sketch, "E23.bottom", {"start": v(51, 21.75) * mm, "end": v(-51, 21.75) * mm});
            skLineSegment(sketch, "E23.top", {"start": v(51, -22.25) * mm, "end": v(-51, -22.25) * mm});
            skLineSegment(sketch, "E23.left", {"start": v(51, 21.75) * mm, "end": v(51, -22.25) * mm});
            skLineSegment(sketch, "E23.right", {"start": v(-51, 21.75) * mm, "end": v(-51, -22.25) * mm});
            skPoint(sketch, "E23.middle", {"position": v(0, -0.25) * mm});
            skSolve(sketch);
        }
        {
            var Q0;
            Q0 = qSketchRegion(id + "F29", true);
            extrude(context, id + "F30", {"entities" : qUnion([Q0]), "depth" : 6 * mm});
        }
        {
            var Q0;
            Q0=makeQuery(id+"F30.opExtrude","CAP_FACE",FACE,{"disambiguationData":[OSD([sQuery(id+"F29.wireOp",EDGE,"E23.bottom"),sQuery(id+"F29.wireOp",EDGE,"E23.top"),sQuery(id+"F29.wireOp",EDGE,"E23.left"),sQuery(id+"F29.wireOp",EDGE,"E23.right")])],"isStart":false});
            var sketch = newSketch(context, id + "F31", { "sketchPlane" : qUnion([Q0])});
            skCircle(sketch, "E24.0", {"center": v(43, 0) * mm, "radius": 2.5 * mm});
            skCircle(sketch, "E24.1", {"center": v(-43, 0) * mm, "radius": 2.5 * mm});
            skSolve(sketch);
        }
        {
            var Q0;
            Q0 = qSketchRegion(id + "F31", true);
            extrude(context, id + "F32", {"entities" : qUnion([Q0]), "operationType" : NewBodyOperationType.REMOVE, "endBound" : BoundingType.THROUGH_ALL, "oppositeDirection" : true, "depth" : 25 * mm});
        }
        {
            var Q0;
            Q0=makeQuery(id+"F30.opExtrude","CAP_FACE",FACE,{"disambiguationData":[OSD([sQuery(id+"F29.wireOp",EDGE,"E23.bottom"),sQuery(id+"F29.wireOp",EDGE,"E23.top"),sQuery(id+"F29.wireOp",EDGE,"E23.left"),sQuery(id+"F29.wireOp",EDGE,"E23.right")])],"isStart":false});
            var sketch = newSketch(context, id + "F33", { "sketchPlane" : qUnion([Q0])});
            skCircle(sketch, "E25", {"center": v(-43, 0) * mm, "radius": 4.5 * mm});
            skCircle(sketch, "E26", {"center": v(43, 0) * mm, "radius": 4.5 * mm});
            skSolve(sketch);
        }
        {
            var Q0;
            Q0 = qSketchRegion(id + "F33", true);
            extrude(context, id + "F34", {"entities" : qUnion([Q0]), "operationType" : NewBodyOperationType.REMOVE, "oppositeDirection" : true, "depth" : 2 * mm});
        }
        {
            var Q0;
            Q0=makeQuery(id+"F30.opExtrude","SWEPT_EDGE",EDGE,{"disambiguationData":[OSD([sQuery(id+"F29.wireOp",EDGE,"E23.top"),sQuery(id+"F29.wireOp",EDGE,"E23.right")])]});
            var Q1;
            Q1=makeQuery(id+"F30.opExtrude","SWEPT_EDGE",EDGE,{"disambiguationData":[OSD([sQuery(id+"F29.wireOp",EDGE,"E23.top"),sQuery(id+"F29.wireOp",EDGE,"E23.left")])]});
            var Q2;
            Q2=makeQuery(id+"F30.opExtrude","SWEPT_EDGE",EDGE,{"disambiguationData":[OSD([sQuery(id+"F29.wireOp",EDGE,"E23.bottom"),sQuery(id+"F29.wireOp",EDGE,"E23.left")])]});
            var Q3;
            Q3=makeQuery(id+"F30.opExtrude","SWEPT_EDGE",EDGE,{"disambiguationData":[OSD([sQuery(id+"F29.wireOp",EDGE,"E23.bottom"),sQuery(id+"F29.wireOp",EDGE,"E23.right")])]});
            chamfer(context, id + "F35", {"entities" : qUnion([Q0, Q1, Q2, Q3]), "width" : 15 * mm, "tangentPropagation" : true});
        }
        {
            var Q0;
            Q0=makeQuery(id+"F30.opExtrude","CAP_FACE",FACE,{"disambiguationData":[OSD([sQuery(id+"F29.wireOp",EDGE,"E23.bottom"),sQuery(id+"F29.wireOp",EDGE,"E23.top"),sQuery(id+"F29.wireOp",EDGE,"E23.left"),sQuery(id+"F29.wireOp",EDGE,"E23.right")])],"isStart":false});
            var sketch = newSketch(context, id + "F36", { "sketchPlane" : qUnion([Q0])});
            skLineSegment(sketch, "E27.bottom", {"start": v(-17.1, -17.1) * mm, "end": v(17.1, -17.1) * mm});
            skLineSegment(sketch, "E27.top", {"start": v(-17.1, 17.1) * mm, "end": v(17.1, 17.1) * mm});
            skLineSegment(sketch, "E27.left", {"start": v(-17.1, -17.1) * mm, "end": v(-17.1, 17.1) * mm});
            skLineSegment(sketch, "E27.right", {"start": v(17.1, -17.1) * mm, "end": v(17.1, 17.1) * mm});
            skPoint(sketch, "E27.middle", {"position": v(0, 0) * mm});
            skSolve(sketch);
        }
        {
            var Q0;
            Q0 = qSketchRegion(id + "F36", true);
            extrude(context, id + "F37", {"entities" : qUnion([Q0]), "operationType" : NewBodyOperationType.REMOVE, "oppositeDirection" : true, "depth" : 2.5 * mm});
        }
        {
            var Q0;
            Q0=makeQuery(id+"F30.opExtrude","CAP_EDGE",EDGE,{"disambiguationData":[OSD([sQuery(id+"F29.wireOp",EDGE,"E23.top")])],"isStart":false});
            var Q1;
            {var subQ0=sQuery(id+"F29.wireOp",EDGE,"E23.right");var subQ1=sQuery(id+"F29.wireOp",EDGE,"E23.top");Q1=makeQuery(id+"F35.opChamfer","BLEND_EDGE",EDGE,{"blendedFrom":[makeQuery(id+"F30.opExtrude","SWEPT_EDGE",EDGE,{"disambiguationData":[OSD([subQ1,subQ0])]}),makeQuery(id+"F30.opExtrude","CAP_FACE",FACE,{"disambiguationData":[OSD([sQuery(id+"F29.wireOp",EDGE,"E23.bottom"),subQ1,sQuery(id+"F29.wireOp",EDGE,"E23.left"),subQ0])],"isStart":false})],"blendedInto":[makeQuery(id+"F30.opExtrude","CAP_FACE",FACE,{"disambiguationData":[OSD([sQuery(id+"F29.wireOp",EDGE,"E23.bottom"),subQ1,sQuery(id+"F29.wireOp",EDGE,"E23.left"),subQ0])],"isStart":false})]});}
            var Q2;
            Q2=makeQuery(id+"F30.opExtrude","CAP_EDGE",EDGE,{"disambiguationData":[OSD([sQuery(id+"F29.wireOp",EDGE,"E23.right")])],"isStart":false});
            var Q3;
            {var subQ0=sQuery(id+"F29.wireOp",EDGE,"E23.right");var subQ1=sQuery(id+"F29.wireOp",EDGE,"E23.bottom");Q3=makeQuery(id+"F35.opChamfer","BLEND_EDGE",EDGE,{"blendedFrom":[makeQuery(id+"F30.opExtrude","SWEPT_EDGE",EDGE,{"disambiguationData":[OSD([subQ1,subQ0])]}),makeQuery(id+"F30.opExtrude","CAP_FACE",FACE,{"disambiguationData":[OSD([subQ1,sQuery(id+"F29.wireOp",EDGE,"E23.top"),sQuery(id+"F29.wireOp",EDGE,"E23.left"),subQ0])],"isStart":false})],"blendedInto":[makeQuery(id+"F30.opExtrude","CAP_FACE",FACE,{"disambiguationData":[OSD([subQ1,sQuery(id+"F29.wireOp",EDGE,"E23.top"),sQuery(id+"F29.wireOp",EDGE,"E23.left"),subQ0])],"isStart":false})]});}
            var Q4;
            Q4=makeQuery(id+"F30.opExtrude","CAP_EDGE",EDGE,{"disambiguationData":[OSD([sQuery(id+"F29.wireOp",EDGE,"E23.bottom")])],"isStart":false});
            var Q5;
            {var subQ0=sQuery(id+"F29.wireOp",EDGE,"E23.left");var subQ1=sQuery(id+"F29.wireOp",EDGE,"E23.bottom");Q5=makeQuery(id+"F35.opChamfer","BLEND_EDGE",EDGE,{"blendedFrom":[makeQuery(id+"F30.opExtrude","SWEPT_EDGE",EDGE,{"disambiguationData":[OSD([subQ1,subQ0])]}),makeQuery(id+"F30.opExtrude","CAP_FACE",FACE,{"disambiguationData":[OSD([subQ1,sQuery(id+"F29.wireOp",EDGE,"E23.top"),subQ0,sQuery(id+"F29.wireOp",EDGE,"E23.right")])],"isStart":false})],"blendedInto":[makeQuery(id+"F30.opExtrude","CAP_FACE",FACE,{"disambiguationData":[OSD([subQ1,sQuery(id+"F29.wireOp",EDGE,"E23.top"),subQ0,sQuery(id+"F29.wireOp",EDGE,"E23.right")])],"isStart":false})]});}
            var Q6;
            Q6=makeQuery(id+"F30.opExtrude","CAP_EDGE",EDGE,{"disambiguationData":[OSD([sQuery(id+"F29.wireOp",EDGE,"E23.left")])],"isStart":false});
            var Q7;
            {var subQ0=sQuery(id+"F29.wireOp",EDGE,"E23.left");var subQ1=sQuery(id+"F29.wireOp",EDGE,"E23.top");Q7=makeQuery(id+"F35.opChamfer","BLEND_EDGE",EDGE,{"blendedFrom":[makeQuery(id+"F30.opExtrude","SWEPT_EDGE",EDGE,{"disambiguationData":[OSD([subQ1,subQ0])]}),makeQuery(id+"F30.opExtrude","CAP_FACE",FACE,{"disambiguationData":[OSD([sQuery(id+"F29.wireOp",EDGE,"E23.bottom"),subQ1,subQ0,sQuery(id+"F29.wireOp",EDGE,"E23.right")])],"isStart":false})],"blendedInto":[makeQuery(id+"F30.opExtrude","CAP_FACE",FACE,{"disambiguationData":[OSD([sQuery(id+"F29.wireOp",EDGE,"E23.bottom"),subQ1,subQ0,sQuery(id+"F29.wireOp",EDGE,"E23.right")])],"isStart":false})]});}
            chamfer(context, id + "F38", {"entities" : qUnion([Q0, Q1, Q2, Q3, Q4, Q5, Q6, Q7]), "width" : 1 * mm, "tangentPropagation" : true});
        }
        {
            var Q0;
            Q0=makeQuery(id+"F30.opExtrude","CAP_FACE",FACE,{"disambiguationData":[OSD([sQuery(id+"F29.wireOp",EDGE,"E23.bottom"),sQuery(id+"F29.wireOp",EDGE,"E23.top"),sQuery(id+"F29.wireOp",EDGE,"E23.left"),sQuery(id+"F29.wireOp",EDGE,"E23.right")])],"isStart":false});
            var sketch = newSketch(context, id + "F39", { "sketchPlane" : qUnion([Q0])});
            skLineSegment(sketch, "E28.bottom", {"start": v(19.83, -16) * mm, "end": v(24.83, -16) * mm});
            skLineSegment(sketch, "E28.top", {"start": v(19.83, 16) * mm, "end": v(24.83, 16) * mm});
            skLineSegment(sketch, "E28.left", {"start": v(19.83, -16) * mm, "end": v(19.83, 16) * mm});
            skLineSegment(sketch, "E28.right", {"start": v(24.83, -16) * mm, "end": v(24.83, 16) * mm});
            skPoint(sketch, "E28.middle", {"position": v(22.33, 0) * mm});
            skPoint(sketch, "E28.middle.positionSnap0", {"position": v(17.1, 0) * mm});
            skPoint(sketch, "E28.centerSnap0", {"position": v(17.1, 0) * mm});
            skLineSegment(sketch, "E29.MirrorCS", {"start": v(-19.83, -16) * mm, "end": v(-24.83, -16) * mm});
            skLineSegment(sketch, "E30.MirrorCS", {"start": v(-24.83, -16) * mm, "end": v(-24.83, 16) * mm});
            skLineSegment(sketch, "E31.MirrorCS", {"start": v(-19.83, -16) * mm, "end": v(-19.83, 16) * mm});
            skLineSegment(sketch, "E32.MirrorCS", {"start": v(-19.83, 16) * mm, "end": v(-24.83, 16) * mm});
            skSolve(sketch);
        }
        {
            var Q0;
            Q0 = qSketchRegion(id + "F39", true);
            extrude(context, id + "F40", {"entities" : qUnion([Q0]), "operationType" : NewBodyOperationType.ADD, "depth" : 3 * mm});
        }
        {
            var Q0;
            Q0=makeQuery(id+"F40.opExtrude","CAP_FACE",FACE,{"disambiguationData":[OSD([sQuery(id+"F39.wireOp",EDGE,"E28.bottom"),sQuery(id+"F39.wireOp",EDGE,"E28.top"),sQuery(id+"F39.wireOp",EDGE,"E28.left"),sQuery(id+"F39.wireOp",EDGE,"E28.right")])],"isStart":false});
            var Q1;
            Q1=makeQuery(id+"F40.opExtrude","CAP_FACE",FACE,{"disambiguationData":[OSD([sQuery(id+"F39.wireOp",EDGE,"E29.MirrorCS"),sQuery(id+"F39.wireOp",EDGE,"E30.MirrorCS"),sQuery(id+"F39.wireOp",EDGE,"E31.MirrorCS"),sQuery(id+"F39.wireOp",EDGE,"E32.MirrorCS")])],"isStart":false});
            chamfer(context, id + "F41", {"entities" : qUnion([Q0, Q1]), "width" : 1 * mm, "tangentPropagation" : true});
        }
        {
            var Q0;
            Q0=makeQuery(id+"F40.opExtrude","CAP_FACE",FACE,{"disambiguationData":[OSD([sQuery(id+"F39.wireOp",EDGE,"E29.MirrorCS"),sQuery(id+"F39.wireOp",EDGE,"E30.MirrorCS"),sQuery(id+"F39.wireOp",EDGE,"E31.MirrorCS"),sQuery(id+"F39.wireOp",EDGE,"E32.MirrorCS")])],"isStart":false});
            var sketch = newSketch(context, id + "F42", { "sketchPlane" : qUnion([Q0])});
            skLineSegment(sketch, "E33.bottom", {"start": v(-48.35, -2.5) * mm, "end": v(48.35, -2.5) * mm});
            skLineSegment(sketch, "E33.top", {"start": v(-48.35, 2.5) * mm, "end": v(48.35, 2.5) * mm});
            skLineSegment(sketch, "E33.left", {"start": v(-48.35, -2.5) * mm, "end": v(-48.35, 2.5) * mm});
            skLineSegment(sketch, "E33.right", {"start": v(48.35, -2.5) * mm, "end": v(48.35, 2.5) * mm});
            skPoint(sketch, "E33.middle", {"position": v(0, 0) * mm});
            skSolve(sketch);
        }
        {
            var Q0;
            Q0 = qSketchRegion(id + "F42", true);
            var Q1;
            Q1=makeQuery(id+"F30.opExtrude","CAP_FACE",FACE,{"disambiguationData":[OSD([sQuery(id+"F29.wireOp",EDGE,"E23.bottom"),sQuery(id+"F29.wireOp",EDGE,"E23.top"),sQuery(id+"F29.wireOp",EDGE,"E23.left"),sQuery(id+"F29.wireOp",EDGE,"E23.right")])],"isStart":false});
            extrude(context, id + "F43", {"entities" : qUnion([Q0]), "operationType" : NewBodyOperationType.REMOVE, "oppositeDirection" : true, "endBoundEntityFace" : qUnion([Q1]), "depth" : 2 * mm});
        }
        {
            var Q0;
            Q0=makeQuery(id+"F37.boolean.opBoolean","COPY",FACE,{"derivedFrom":makeQuery(id+"F37.opExtrude","CAP_FACE",FACE,{"disambiguationData":[OSD([sQuery(id+"F36.wireOp",EDGE,"E27.bottom"),sQuery(id+"F36.wireOp",EDGE,"E27.top"),sQuery(id+"F36.wireOp",EDGE,"E27.left"),sQuery(id+"F36.wireOp",EDGE,"E27.right")])],"isStart":false})});
            var sketch = newSketch(context, id + "F44", { "sketchPlane" : qUnion([Q0])});
            skLineSegment(sketch, "E34.0", {"start": v(14.1, 14.1) * mm, "end": v(-14.1, 14.1) * mm});
            skLineSegment(sketch, "E34.1", {"start": v(14.1, -14.1) * mm, "end": v(14.1, 14.1) * mm});
            skLineSegment(sketch, "E34.2", {"start": v(-14.1, -14.1) * mm, "end": v(14.1, -14.1) * mm});
            skLineSegment(sketch, "E34.3", {"start": v(-14.1, 14.1) * mm, "end": v(-14.1, -14.1) * mm});
            skSolve(sketch);
        }
        {
            var Q0;
            Q0 = qSketchRegion(id + "F44", true);
            extrude(context, id + "F45", {"entities" : qUnion([Q0]), "operationType" : NewBodyOperationType.REMOVE, "oppositeDirection" : true, "depth" : 1.2 * mm});
        }
        {
            var Q0;
            Q0=makeQuery(id+"F30.opExtrude","CAP_FACE",FACE,{"disambiguationData":[OSD([sQuery(id+"F29.wireOp",EDGE,"E23.bottom"),sQuery(id+"F29.wireOp",EDGE,"E23.top"),sQuery(id+"F29.wireOp",EDGE,"E23.left"),sQuery(id+"F29.wireOp",EDGE,"E23.right")])],"isStart":true});
            var sketch = newSketch(context, id + "F46", { "sketchPlane" : qUnion([Q0])});
            skCircle(sketch, "E35.0", {"center": v(-11.15, 0) * mm, "radius": 1.5 * mm});
            skSolve(sketch);
        }
        {
            var Q0;
            Q0 = qSketchRegion(id + "F46", true);
            extrude(context, id + "F47", {"entities" : qUnion([Q0]), "operationType" : NewBodyOperationType.REMOVE, "endBound" : BoundingType.THROUGH_ALL, "oppositeDirection" : true, "depth" : 25 * mm});
        }
        {
            var Q0;
            Q0=makeQuery(id+"F30.opExtrude","CAP_FACE",FACE,{"disambiguationData":[OSD([sQuery(id+"F29.wireOp",EDGE,"E23.bottom"),sQuery(id+"F29.wireOp",EDGE,"E23.top"),sQuery(id+"F29.wireOp",EDGE,"E23.left"),sQuery(id+"F29.wireOp",EDGE,"E23.right")])],"isStart":true});
            var sketch = newSketch(context, id + "F48", { "sketchPlane" : qUnion([Q0])});
            skCircle(sketch, "E36", {"center": v(-11.15, 0) * mm, "radius": 7.5 * mm});
            skCircle(sketch, "E37", {"center": v(-11.15, 0) * mm, "radius": 9.5 * mm});
            skSolve(sketch);
        }
        {
            var Q0;
            Q0 = qSketchRegion(id + "F48", true);
            extrude(context, id + "F49", {"entities" : qUnion([Q0]), "operationType" : NewBodyOperationType.REMOVE, "oppositeDirection" : true, "depth" : 1.2 * mm});
        }
        {
            var Q0;
            Q0=makeQuery(id+"F49.boolean.opBoolean","COPY",FACE,{"derivedFrom":makeQuery(id+"F49.opExtrude","CAP_FACE",FACE,{"disambiguationData":[OSD([sQuery(id+"F48.wireOp",EDGE,"E36"),sQuery(id+"F48.wireOp",EDGE,"E37")])],"isStart":false})});
            fillet(context, id + "F50", {"entities" : qUnion([Q0]), "radius" : 0.7 * mm, "tangentPropagation" : true, "allowEdgeOverflow" : false});
        }
    });
